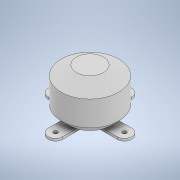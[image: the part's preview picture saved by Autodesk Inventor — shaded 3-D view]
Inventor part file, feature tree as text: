
AUTODESK INVENTOR PART (.ipt)
format: ipt  version: 2020 (Build 240168000, 168)  size: 151,552 bytes
history: native  units: in
note: dims shown in document units (in); Inventor stores cm internally (conversion verified against a paired STEP export)
features: sketch x2, revolve x1, extrude x1
ambient origin geometry x8: Origin, YZ Plane, XZ Plane, XY Plane, X Axis, Y Axis, Z Axis, Center Point
bodies: Solid1 (feature_tree)
feature tree (4):
  revolve  "Revolution1"  [1 undecoded]
  extrude  "Extrusion1"  Depth=0.076in
  sketch  "Sketch1"  dims[d0=0.7in d1=1.3in]
  sketch  "Sketch2"  dims[d2=0.905in d3=0.22in d4=0.785in d5=0.425in d6=90.0deg d7=0.465in d8=2.173in d9=0.1275in d10=0.076in d11=0.0in]
note: 1 required parameter value undecoded (feature->parameter linkage not recoverable at this tier; creation-order binding heuristic only, values carry confidence <= 0.55)
